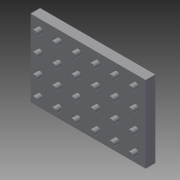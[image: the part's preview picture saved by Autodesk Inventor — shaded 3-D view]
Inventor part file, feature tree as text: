
AUTODESK INVENTOR PART (.ipt)
format: ipt  version: 2015 (Build 190159000, 159)  size: 130,560 bytes
history: native  units: in
note: dims shown in document units (in); Inventor stores cm internally (conversion verified against a paired STEP export)
features: extrude x2, sketch x2
ambient origin geometry x8: Origin, YZ Plane, XZ Plane, XY Plane, X Axis, Y Axis, Z Axis, Center Point
bodies: Solid1 (feature_tree)
feature tree (4):
  extrude  "Extrusion1"  Depth=4.0in
  extrude  "Extrusion2"  Depth=0.3in
  sketch  "Sketch1"  dims[d0=6.0in d1=4.0in]
  sketch  "Sketch2"  dims[d2=0.5in d3=0.0in d4=0.3in d5=0.5in d6=0.5in d7=1.5748in d9=1.0in d10=2.3622in d12=1.0in d15=0.3in d16=0.0in]
